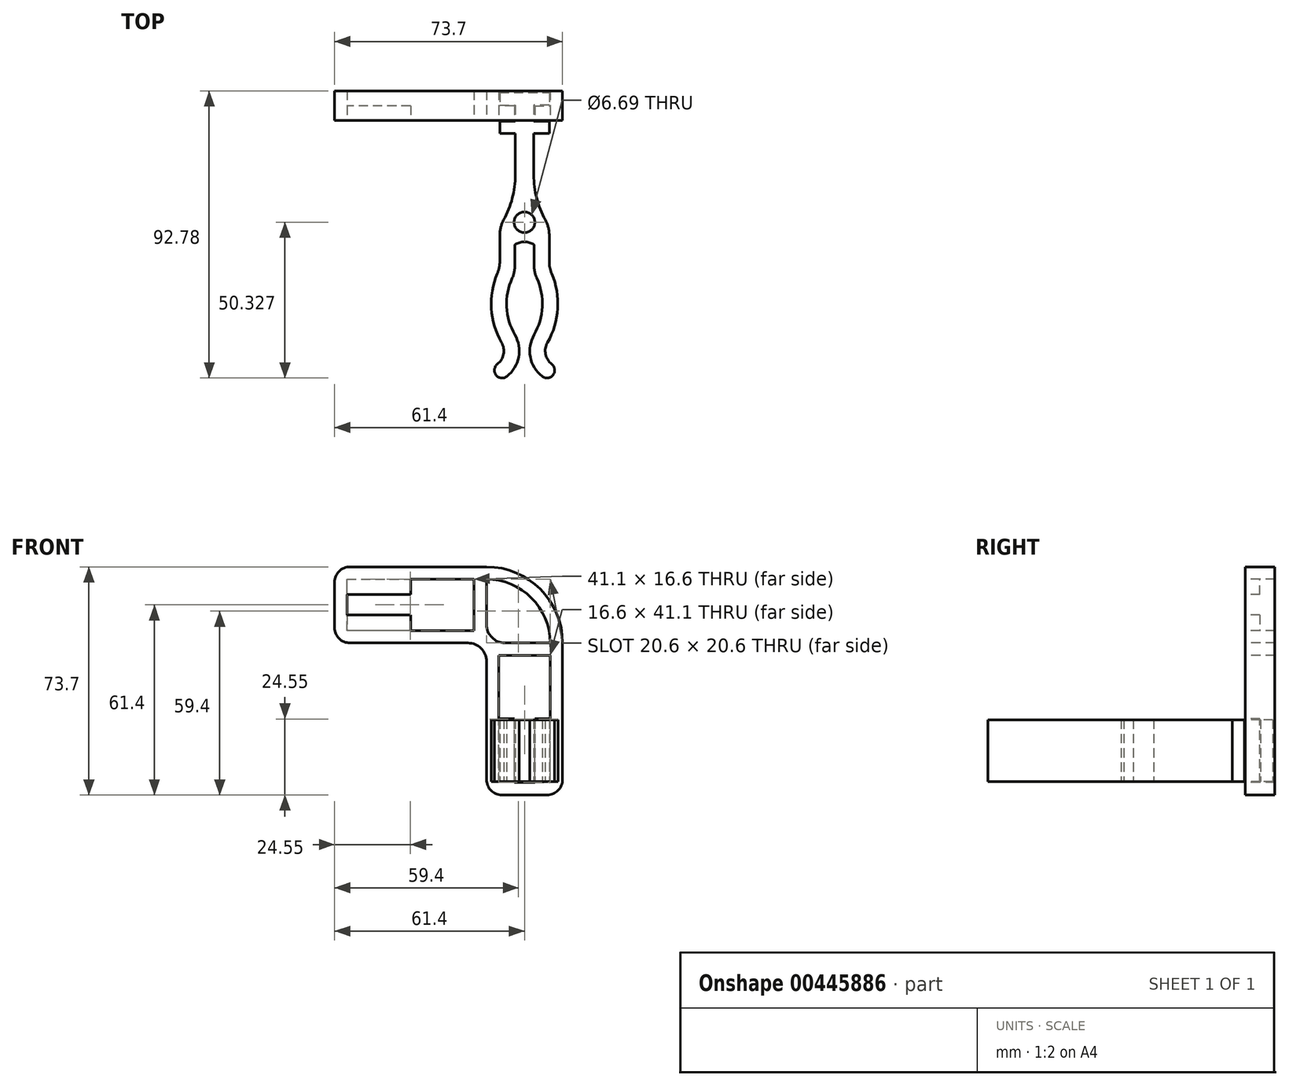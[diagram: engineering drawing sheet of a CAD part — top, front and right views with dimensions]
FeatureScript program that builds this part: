
annotation { "Feature Type Name" : "Feature", "Feature Type Description" : "" }
export const myFeature = defineFeature(function(context is Context, id is Id, definition is map)
    precondition{}
    {
        {
            var Q0;
            Q0=qCreatedBy(makeId("Top.planeOp"),FACE);
            var sketch = newSketch(context, id + "F0", { "sketchPlane" : qUnion([Q0])});
            skLineSegment(sketch, "E0", {"start": v(0, 0) * mm, "end": v(0, -4) * mm});
            skLineSegment(sketch, "E1", {"start": v(0, -4) * mm, "end": v(5, -4) * mm});
            skLineSegment(sketch, "E2", {"start": v(5, -4) * mm, "end": v(5, -9.2) * mm});
            skLineSegment(sketch, "E3", {"start": v(5, -9.2) * mm, "end": v(0, -9.2) * mm});
            skLineSegment(sketch, "E4", {"start": v(0, -9.2) * mm, "end": v(0, -13.2) * mm});
            skLineSegment(sketch, "E5", {"start": v(0, -13.2) * mm, "end": v(5, -13.2) * mm});
            skLineSegment(sketch, "E6", {"start": v(5, -13.2) * mm, "end": v(5, -43.2) * mm});
            skLineSegment(sketch, "E7", {"start": v(5, -43.2) * mm, "end": v(0, -43.2) * mm, "construction": true});
            skLineSegment(sketch, "E8", {"start": v(0, -43.2) * mm, "end": v(0, -56.74) * mm});
            skLineSegment(sketch, "E9", {"start": v(0, 0) * mm, "end": v(8, 0) * mm});
            skLineSegment(sketch, "E10", {"start": v(8, 0) * mm, "end": v(8, -48.2) * mm});
            skLineSegment(sketch, "E11", {"start": v(8, -48.2) * mm, "end": v(4.9, -48.2) * mm, "construction": true});
            skArc(sketch, "E12", {"start": v(0, -43.2) * mm, "mid": v(3.72, -35.28) * mm, "end": v(5, -26.62) * mm});
            skLineSegment(sketch, "E13", {"start": v(4.9, -48.2) * mm, "end": v(4.9, -58.2) * mm});
            skLineSegment(sketch, "E14", {"start": v(4.9, -58.2) * mm, "end": v(4.9, -78.2) * mm, "construction": true});
            skLineSegment(sketch, "E15", {"start": v(4.9, -78.2) * mm, "end": v(0, -78.2) * mm, "construction": true});
            skLineSegment(sketch, "E16", {"start": v(4.9, -68.2) * mm, "end": v(11.66, -68.2) * mm, "construction": true});
            skPoint(sketch, "E16.endSnap0", {"position": v(4.9, -68.2) * mm});
            skArc(sketch, "E17", {"start": v(4.9, -58.2) * mm, "mid": v(2.22, -68.2) * mm, "end": v(4.9, -78.2) * mm});
            skArc(sketch, "E18", {"start": v(0, -56.74) * mm, "mid": v(-2.77, -68.8) * mm, "end": v(0.57, -80.7) * mm});
            skArc(sketch, "E19", {"start": v(8, -48.2) * mm, "mid": v(6.4, -48.42) * mm, "end": v(4.9, -49.06) * mm});
            skArc(sketch, "E20", {"start": v(4.9, -78.2) * mm, "mid": v(6.1, -85.4) * mm, "end": v(2.3, -91.65) * mm});
            skLineSegment(sketch, "E21", {"start": v(6.3, -82.88) * mm, "end": v(6.3, -110.36) * mm, "construction": true});
            skArc(sketch, "E22", {"start": v(0.57, -80.7) * mm, "mid": v(1.2, -84.46) * mm, "end": v(-0.79, -87.71) * mm});
            skArc(sketch, "E23", {"start": v(2.3, -91.65) * mm, "mid": v(-1.21, -91.22) * mm, "end": v(-0.79, -87.71) * mm});
            skPoint(sketch, "E24.orphan", {"position": v(4.9, -86.23) * mm});
            skCircle(sketch, "E25", {"center": v(8, -41.85) * mm, "radius": 3.35 * mm});
            skSolve(sketch);
        }
        {
            var Q0;
            Q0=makeQuery(id+"F0.imprint","IMPRINT",FACE,{"disambiguationData":[TD([[makeQuery(id+"F0.imprint","IMPRINT",EDGE,{"derivedFrom":sQuery(id+"F0.wireOp",EDGE,"E0")}),1.0]])]});
            var Q1;
            Q1=makeQuery(id+"F0.imprint","IMPRINT",FACE,{"disambiguationData":[TD([[makeQuery(id+"F0.imprint","IMPRINT",EDGE,{"derivedFrom":sQuery(id+"F0.wireOp",EDGE,"E8")}),1.0]])]});
            extrude(context, id + "F1", {"entities" : qUnion([Q0, Q1]), "depth" : 20 * mm});
        }
        {
            var Q0;
            Q0=makeQuery(id+"F1.opExtrude","SWEPT_EDGE",EDGE,{"disambiguationData":[OSD([sQuery(id+"F0.wireOp",EDGE,"E13"),sQuery(id+"F0.wireOp",EDGE,"E17")])]});
            var Q1;
            Q1=makeQuery(id+"F1.opExtrude","SWEPT_EDGE",EDGE,{"disambiguationData":[OSD([sQuery(id+"F0.wireOp",EDGE,"E8"),sQuery(id+"F0.wireOp",EDGE,"E18")])]});
            var Q2;
            Q2=makeQuery(id+"F1.opExtrude","SWEPT_EDGE",EDGE,{"disambiguationData":[OSD([sQuery(id+"F0.wireOp",EDGE,"E8"),sQuery(id+"F0.wireOp",EDGE,"E12")])]});
            fillet(context, id + "F2", {"entities" : qUnion([Q0, Q1, Q2]), "radius" : 10 * mm, "tangentPropagation" : true, "allowEdgeOverflow" : false});
        }
        {
            var Q0;
            Q0=makeQuery(id+"F1.opExtrude","SWEPT_BODY",BODY,{"disambiguationData":[OSD([sQuery(id+"F0.wireOp",EDGE,"E0"),sQuery(id+"F0.wireOp",EDGE,"E1"),sQuery(id+"F0.wireOp",EDGE,"E2"),sQuery(id+"F0.wireOp",EDGE,"E3"),sQuery(id+"F0.wireOp",EDGE,"E4"),sQuery(id+"F0.wireOp",EDGE,"E5"),sQuery(id+"F0.wireOp",EDGE,"E6"),sQuery(id+"F0.wireOp",EDGE,"E8"),sQuery(id+"F0.wireOp",EDGE,"E9"),sQuery(id+"F0.wireOp",EDGE,"E10"),sQuery(id+"F0.wireOp",EDGE,"E12"),sQuery(id+"F0.wireOp",EDGE,"E13"),sQuery(id+"F0.wireOp",EDGE,"E17"),sQuery(id+"F0.wireOp",EDGE,"E18"),sQuery(id+"F0.wireOp",EDGE,"zQibL5ya-3dB8-KEST-48bZ-U9P0G53MtYtZ"),sQuery(id+"F0.wireOp",EDGE,"E19")])]});
            var Q1;
            Q1=makeQuery(id+"F1.opExtrude","SWEPT_FACE",FACE,{"disambiguationData":[OSD([sQuery(id+"F0.wireOp",EDGE,"E10")])]});
            mirror(context, id + "F3", {"operationType" : NewBodyOperationType.ADD, "entities" : qUnion([Q0]), "mirrorPlane" : qUnion([Q1])});
        }
        {
            var Q0;
            Q0=makeQuery(id+"F3.opPattern","COPY",FACE,{"derivedFrom":makeQuery(id+"F1.opExtrude","SWEPT_FACE",FACE,{"disambiguationData":[OSD([sQuery(id+"F0.wireOp",EDGE,"E3")])]}),"instanceName":"1"});
            cPlane(context, id + "F4", {"entities" : qUnion([Q0]), "cplaneType" : CPlaneType.OFFSET, "offset" : 0.3 * mm, "width" : 150 * mm, "height" : 150 * mm});
        }
        {
            var Q0;
            Q0=qCreatedBy(id+"F4.planeOp",FACE);
            var sketch = newSketch(context, id + "F5", { "sketchPlane" : qUnion([Q0])});
            skLineSegment(sketch, "E26.0", {"start": v(-11, 20) * mm, "end": v(-11, 0) * mm, "construction": true});
            skLineSegment(sketch, "E27.0", {"start": v(-5, 20) * mm, "end": v(-5, 0) * mm, "construction": true});
            skLineSegment(sketch, "E28.bottom", {"start": v(-4.7, -0.3) * mm, "end": v(-11.3, -0.3) * mm});
            skLineSegment(sketch, "E28.top", {"start": v(-4.7, 20.3) * mm, "end": v(-11.3, 20.3) * mm});
            skLineSegment(sketch, "E28.left", {"start": v(-4.7, -0.3) * mm, "end": v(-4.7, 20.3) * mm});
            skLineSegment(sketch, "E28.right", {"start": v(-11.3, -0.3) * mm, "end": v(-11.3, 20.3) * mm});
            skLineSegment(sketch, "E29.0", {"start": v(0, 20) * mm, "end": v(0, 0) * mm, "construction": true});
            skLineSegment(sketch, "E30.0", {"start": v(-16, 20) * mm, "end": v(-16, 0) * mm, "construction": true});
            skLineSegment(sketch, "E31.bottom", {"start": v(0.3, 20.3) * mm, "end": v(-16.3, 20.3) * mm});
            skLineSegment(sketch, "E31.top", {"start": v(0.3, 40.8) * mm, "end": v(-16.3, 40.8) * mm});
            skLineSegment(sketch, "E31.left", {"start": v(0.3, 20.3) * mm, "end": v(0.3, 40.8) * mm});
            skLineSegment(sketch, "E31.right", {"start": v(-16.3, 20.3) * mm, "end": v(-16.3, 40.8) * mm});
            skLineSegment(sketch, "E32.bottom", {"start": v(4.3, -4.3) * mm, "end": v(-20.3, -4.3) * mm});
            skLineSegment(sketch, "E32.top", {"start": v(-1.7, 44.8) * mm, "end": v(-16.3, 44.8) * mm});
            skLineSegment(sketch, "E32.left", {"start": v(4.3, -4.3) * mm, "end": v(4.3, 38.8) * mm});
            skLineSegment(sketch, "E32.right", {"start": v(-20.3, -4.3) * mm, "end": v(-20.3, 44.8) * mm});
            skArc(sketch, "E33", {"start": v(-20.3, 44.8) * mm, "mid": v(-13.1, 62.2) * mm, "end": v(4.3, 69.4) * mm});
            skLineSegment(sketch, "E34", {"start": v(4.3, 44.8) * mm, "end": v(-13.1, 62.2) * mm, "construction": true});
            skLineSegment(sketch, "E35.MirrorCS", {"start": v(4.3, 50.8) * mm, "end": v(4.3, 65.4) * mm});
            skLineSegment(sketch, "E36.MirrorCS", {"start": v(53.4, 69.4) * mm, "end": v(4.3, 69.4) * mm});
            skLineSegment(sketch, "E37.MirrorCS", {"start": v(53.4, 44.8) * mm, "end": v(10.3, 44.8) * mm});
            skLineSegment(sketch, "E38.MirrorCS", {"start": v(53.4, 44.8) * mm, "end": v(53.4, 69.4) * mm});
            skLineSegment(sketch, "E39.MirrorCS", {"start": v(28.8, 65.4) * mm, "end": v(8.3, 65.4) * mm});
            skLineSegment(sketch, "E40.MirrorCS", {"start": v(28.8, 48.8) * mm, "end": v(8.3, 48.8) * mm});
            skLineSegment(sketch, "E41.MirrorCS", {"start": v(28.8, 48.8) * mm, "end": v(28.8, 65.4) * mm});
            skLineSegment(sketch, "E42.MirrorCS", {"start": v(49.4, 53.8) * mm, "end": v(28.8, 53.8) * mm});
            skLineSegment(sketch, "E43.MirrorCS", {"start": v(49.4, 60.4) * mm, "end": v(28.8, 60.4) * mm});
            skLineSegment(sketch, "E44.MirrorCS", {"start": v(49.4, 53.8) * mm, "end": v(49.4, 60.4) * mm});
            skLineSegment(sketch, "E45.MirrorCS", {"start": v(8.3, 48.8) * mm, "end": v(8.3, 65.4) * mm});
            skLineSegment(sketch, "E46.bottom", {"start": v(28.8, 53.8) * mm, "end": v(49.4, 53.8) * mm});
            skLineSegment(sketch, "E46.top", {"start": v(28.8, 48.8) * mm, "end": v(49.4, 48.8) * mm});
            skLineSegment(sketch, "E46.left", {"start": v(28.8, 53.8) * mm, "end": v(28.8, 48.8) * mm});
            skLineSegment(sketch, "E46.right", {"start": v(49.4, 53.8) * mm, "end": v(49.4, 48.8) * mm});
            skLineSegment(sketch, "E47.top", {"start": v(49.4, 65.4) * mm, "end": v(28.8, 65.4) * mm});
            skLineSegment(sketch, "E47.left", {"start": v(49.4, 60.4) * mm, "end": v(49.4, 65.4) * mm});
            skLineSegment(sketch, "E47.right", {"start": v(28.8, 60.4) * mm, "end": v(28.8, 65.4) * mm});
            skLineSegment(sketch, "E48.MirrorCS", {"start": v(0.3, 20.3) * mm, "end": v(0.3, -0.3) * mm});
            skLineSegment(sketch, "E49.MirrorCS", {"start": v(-4.7, -0.3) * mm, "end": v(0.3, -0.3) * mm});
            skLineSegment(sketch, "E50.MirrorCS", {"start": v(-11.3, -0.3) * mm, "end": v(-16.3, -0.3) * mm});
            skLineSegment(sketch, "E51.MirrorCS", {"start": v(-16.3, -0.3) * mm, "end": v(-16.3, 20.3) * mm});
            skArc(sketch, "E52", {"start": v(-16.3, 44.8) * mm, "mid": v(-10.27, 59.37) * mm, "end": v(4.3, 65.4) * mm});
            skPoint(sketch, "E53.orphan", {"position": v(4.3, 69.4) * mm});
            skArc(sketch, "E54.filletArc", {"start": v(10.3, 44.8) * mm, "mid": v(6.06, 43.04) * mm, "end": v(4.3, 38.8) * mm});
            skArc(sketch, "E55.filletArc", {"start": v(-1.7, 44.8) * mm, "mid": v(2.54, 46.56) * mm, "end": v(4.3, 50.8) * mm});
            skSolve(sketch);
        }
        {
            var Q0;
            Q0=makeQuery(id+"F5.imprint","IMPRINT",FACE,{"disambiguationData":[TD([[makeQuery(id+"F5.imprint","IMPRINT",EDGE,{"derivedFrom":sQuery(id+"F5.wireOp",EDGE,"E28.bottom")}),1.0]])]});
            extrude(context, id + "F6", {"entities" : qUnion([Q0]), "depth" : 9.5 * mm, "offsetDistance" : 25 * mm});
        }
        {
            var Q0;
            {var subQ2=sQuery(id+"F5.wireOp",EDGE,"E42.MirrorCS");Q0=makeQuery(id+"F5.imprint","IMPRINT",FACE,{"disambiguationData":[TD([[makeQuery(id+"F5.imprint","IMPRINT",EDGE,{"derivedFrom":subQ2}),1.0]])]});}
            var Q1;
            {var subQ2=sQuery(id+"F5.wireOp",EDGE,"E43.MirrorCS");Q1=makeQuery(id+"F5.imprint","IMPRINT",FACE,{"disambiguationData":[TD([[makeQuery(id+"F5.imprint","IMPRINT",EDGE,{"derivedFrom":subQ2}),-1.0]])]});}
            var Q2;
            {var subQ0=sQuery(id+"F5.wireOp",EDGE,"E28.right");Q2=makeQuery(id+"F5.imprint","IMPRINT",FACE,{"disambiguationData":[TD([[makeQuery(id+"F5.imprint","IMPRINT",EDGE,{"derivedFrom":subQ0}),1.0]])]});}
            var Q3;
            {var subQ0=sQuery(id+"F5.wireOp",EDGE,"E28.left");Q3=makeQuery(id+"F5.imprint","IMPRINT",FACE,{"disambiguationData":[TD([[makeQuery(id+"F5.imprint","IMPRINT",EDGE,{"derivedFrom":subQ0}),-1.0]])]});}
            extrude(context, id + "F7", {"entities" : qUnion([Q0, Q1, Q2, Q3]), "operationType" : NewBodyOperationType.ADD, "depth" : 4.7 * mm, "offsetDistance" : 25 * mm});
        }
        {
            var Q0;
            Q0=makeQuery(id+"F6.opExtrude","SWEPT_EDGE",EDGE,{"disambiguationData":[OSD([sQuery(id+"F5.wireOp",EDGE,"E37.MirrorCS"),sQuery(id+"F5.wireOp",EDGE,"E38.MirrorCS")])]});
            var Q1;
            Q1=makeQuery(id+"F6.opExtrude","SWEPT_EDGE",EDGE,{"disambiguationData":[OSD([sQuery(id+"F5.wireOp",EDGE,"E36.MirrorCS"),sQuery(id+"F5.wireOp",EDGE,"E38.MirrorCS")])]});
            var Q2;
            Q2=makeQuery(id+"F6.opExtrude","SWEPT_EDGE",EDGE,{"disambiguationData":[OSD([sQuery(id+"F5.wireOp",EDGE,"E32.bottom"),sQuery(id+"F5.wireOp",EDGE,"E32.right")])]});
            var Q3;
            Q3=makeQuery(id+"F6.opExtrude","SWEPT_EDGE",EDGE,{"disambiguationData":[OSD([sQuery(id+"F5.wireOp",EDGE,"E32.bottom"),sQuery(id+"F5.wireOp",EDGE,"E32.left")])]});
            fillet(context, id + "F8", {"entities" : qUnion([Q0, Q1, Q2, Q3]), "radius" : 5 * mm, "tangentPropagation" : true, "allowEdgeOverflow" : false});
        }
    });
